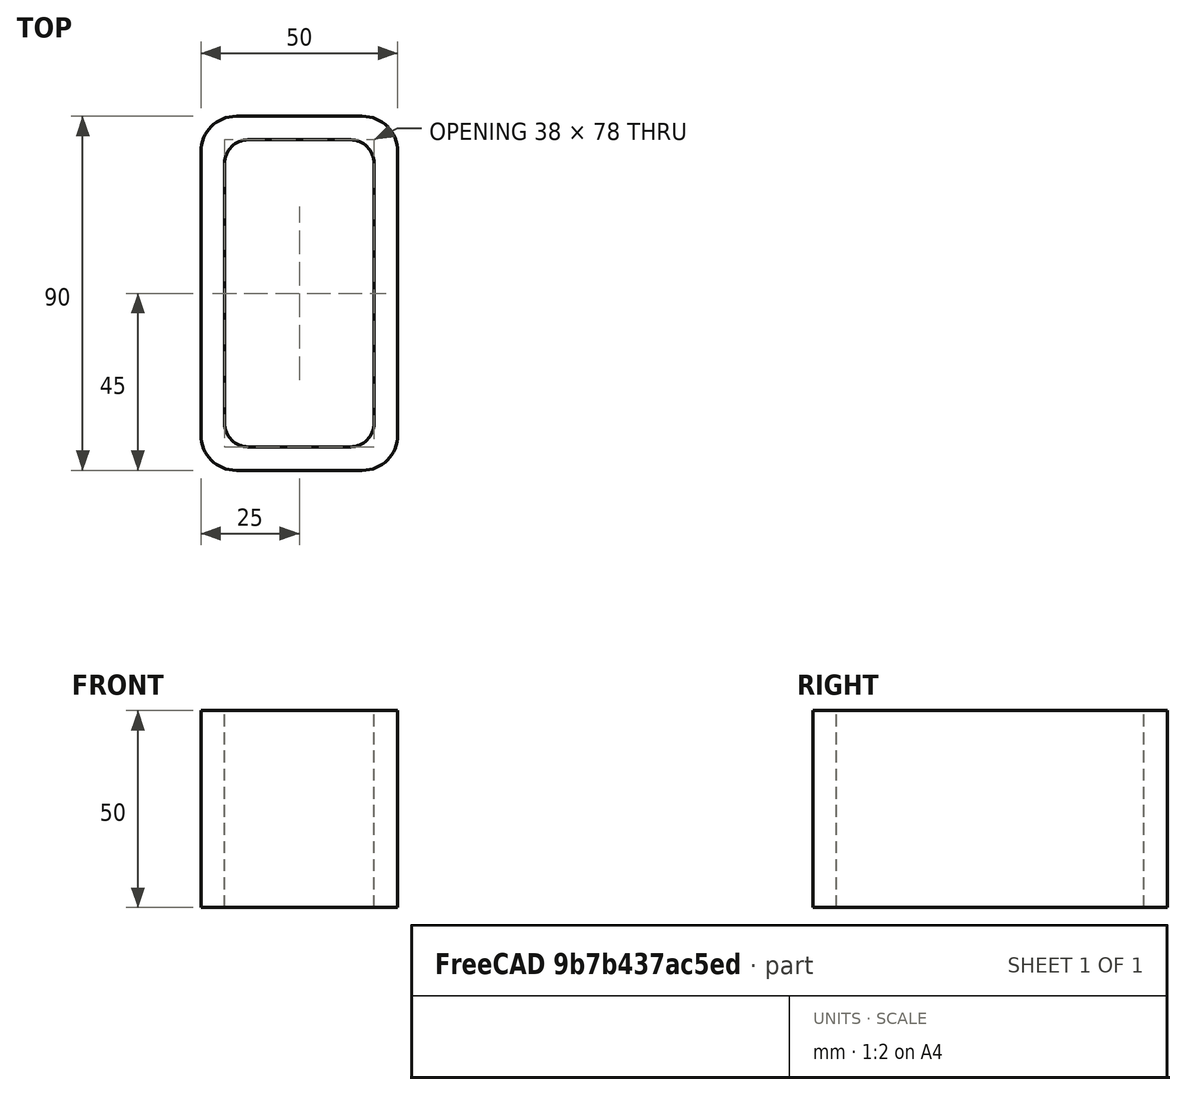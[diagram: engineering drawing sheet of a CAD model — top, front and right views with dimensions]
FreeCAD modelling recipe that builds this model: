
FCSTD DOCUMENT  (FreeCAD 0.15R4671 (Git))
Label: Rectangular hollow section 90x50x6 EN10219 S235JRH
License: All rights reserved
LicenseURL: http://en.wikipedia.org/wiki/All_rights_reserved
objects: Sketcher::SketchObject×1, Part::Extrusion×1
note: 2 computed .brp shape members not serialized (recipe doc carries the construction recipe); baked Part::Feature solids carry a one-line shape summary decoded from their .brp

FEATURE [Sketcher::SketchObject] Sketch
  sketch-geometry (16):
    g0: LineSegment StartX=-13 StartY=39 StartZ=0 EndX=13 EndY=39 EndZ=0
    g1: LineSegment StartX=19 StartY=33 StartZ=0 EndX=19 EndY=-33 EndZ=0
    g2: LineSegment StartX=13 StartY=-39 StartZ=0 EndX=-13 EndY=-39 EndZ=0
    g3: LineSegment StartX=-19 StartY=-33 StartZ=0 EndX=-19 EndY=33 EndZ=0
    g4: LineSegment StartX=-16 StartY=45 StartZ=0 EndX=16 EndY=45 EndZ=0
    g5: LineSegment StartX=25 StartY=36 StartZ=0 EndX=25 EndY=-36 EndZ=0
    g6: LineSegment StartX=16 StartY=-45 StartZ=0 EndX=-16 EndY=-45 EndZ=0
    g7: LineSegment StartX=-25 StartY=-36 StartZ=0 EndX=-25 EndY=36 EndZ=0
    g8: ArcOfCircle CenterX=-13 CenterY=33 CenterZ=0 NormalX=0 NormalY=0 NormalZ=1 Radius=6 StartAngle=1.5708 EndAngle=3.14159
    g9: ArcOfCircle CenterX=13 CenterY=33 CenterZ=0 NormalX=0 NormalY=0 NormalZ=1 Radius=6 StartAngle=0 EndAngle=1.5708
    g10: ArcOfCircle CenterX=13 CenterY=-33 CenterZ=0 NormalX=0 NormalY=0 NormalZ=1 Radius=6 StartAngle=4.71239 EndAngle=6.28319
    g11: ArcOfCircle CenterX=-13 CenterY=-33 CenterZ=0 NormalX=0 NormalY=0 NormalZ=1 Radius=6 StartAngle=3.14159 EndAngle=4.71239
    g12: ArcOfCircle CenterX=16 CenterY=36 CenterZ=0 NormalX=0 NormalY=0 NormalZ=1 Radius=9 StartAngle=0 EndAngle=1.5708
    g13: ArcOfCircle CenterX=16 CenterY=-36 CenterZ=0 NormalX=0 NormalY=0 NormalZ=1 Radius=9 StartAngle=4.71239 EndAngle=6.28319
    g14: ArcOfCircle CenterX=-16 CenterY=-36 CenterZ=0 NormalX=0 NormalY=0 NormalZ=1 Radius=9 StartAngle=3.14159 EndAngle=4.71239
    g15: ArcOfCircle CenterX=-16 CenterY=36 CenterZ=0 NormalX=0 NormalY=0 NormalZ=1 Radius=9 StartAngle=1.5708 EndAngle=3.14159
  constraints (36):
    c: Horizontal(g2)
    c: Vertical(g3)
    c: Horizontal(g6)
    c: Vertical(g7)
    c: Tangent(g3,g8) = 1.5708
    c: Tangent(g0,g8) = 1.5708
    c: Tangent(g0,g9) = 1.5708
    c: Tangent(g1,g9) = 1.5708
    c: Tangent(g1,g10) = 1.5708
    c: Tangent(g2,g10) = 1.5708
    c: Tangent(g2,g11) = 1.5708
    c: Tangent(g3,g11) = 1.5708
    c: Tangent(g4,g12) = 1.5708
    c: Tangent(g5,g12) = 1.5708
    c: Tangent(g5,g13) = 1.5708
    c: Tangent(g6,g13) = 1.5708
    c: Tangent(g6,g14) = 1.5708
    c: Tangent(g7,g14) = 1.5708
    c: Tangent(g7,g15) = 1.5708
    c: Tangent(g4,g15) = 1.5708
    c: Equal(g9,g8)
    c: Equal(g9,g11)
    c: Equal(g9,g10)
    c: Equal(g12,g15)
    c: Equal(g12,g14)
    c: Equal(g12,g13)
    c: Symmetric(g4,g6,g-1)
    c: Symmetric(g7,g5,g-2)
    c: DistanceY(g4,g6) = -90
    c: DistanceX(g7,g5) = 50
    c: Symmetric(g3,g1,g-2)
    c: Symmetric(g0,g2,g-1)
    c: DistanceY(g0,g4) = 6
    c: DistanceX(g5,g1) = -6
    c: Radius(g9) = 6
    c: Radius(g12) = 9
FEATURE [Part::Extrusion] Extrude  label="Rectangular hollow section 90x50x6 EN10219 S235JRH"
  Base = -> Sketch
  Dir = (0,0,50)
  Solid = true
